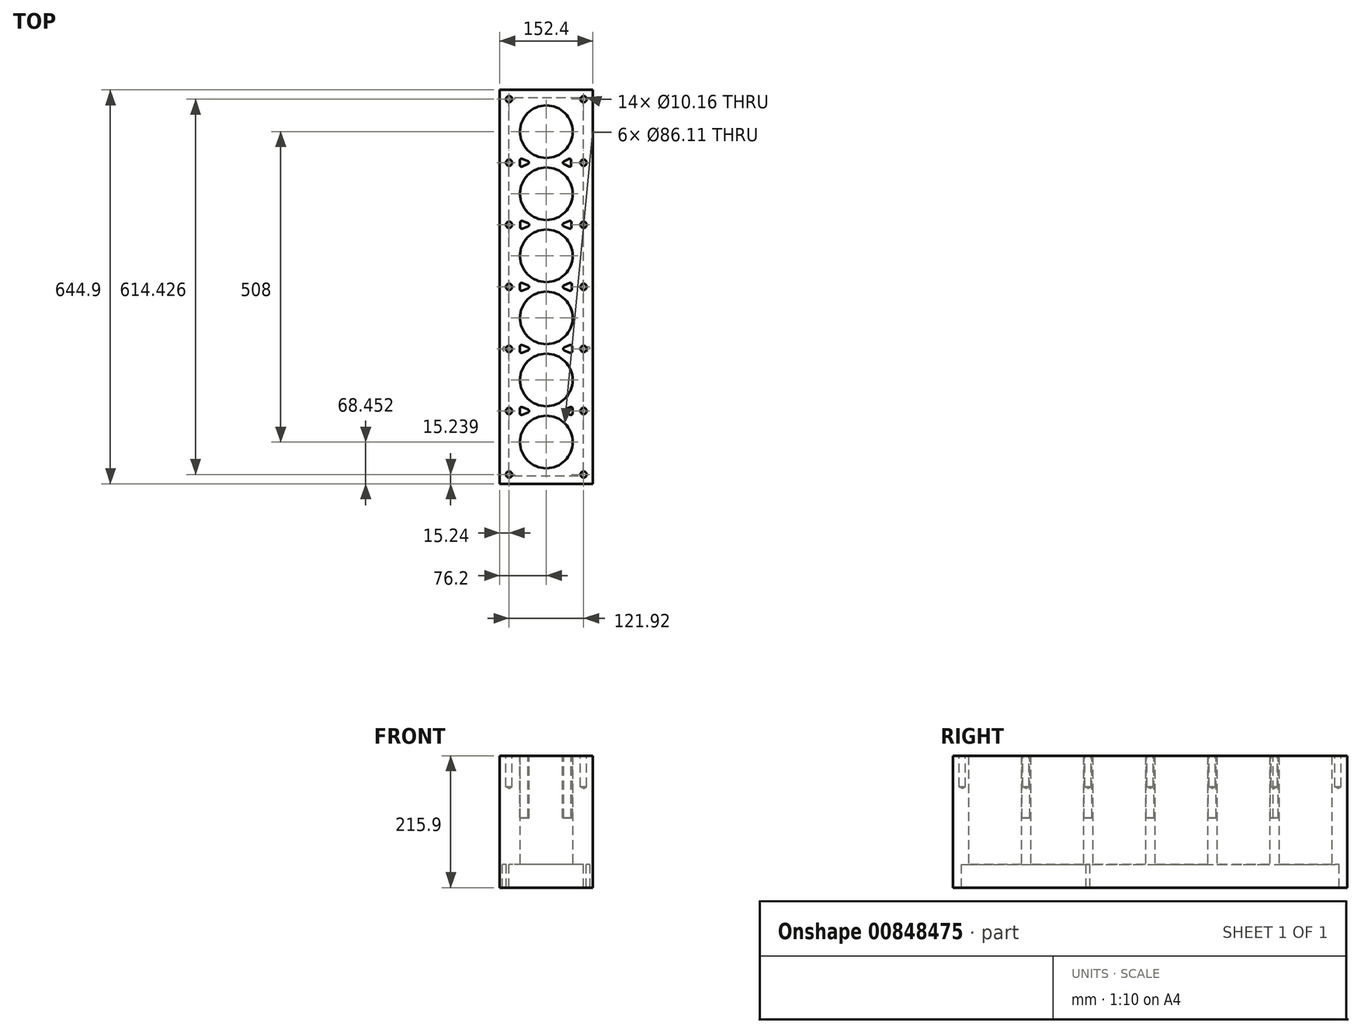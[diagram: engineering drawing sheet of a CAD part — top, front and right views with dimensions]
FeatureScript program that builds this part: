
annotation { "Feature Type Name" : "Feature", "Feature Type Description" : "" }
export const myFeature = defineFeature(function(context is Context, id is Id, definition is map)
    precondition{}
    {
        {
            var Q0;
            Q0=qCreatedBy(makeId("Top.planeOp"),FACE);
            var sketch = newSketch(context, id + "F0", { "sketchPlane" : qUnion([Q0])});
            skLineSegment(sketch, "E0.bottom", {"start": v(-76.2, 345.4) * mm, "end": v(76.2, 345.4) * mm});
            skLineSegment(sketch, "E0.top", {"start": v(-76.2, -299.5) * mm, "end": v(76.2, -299.5) * mm});
            skLineSegment(sketch, "E0.left", {"start": v(-76.2, 345.4) * mm, "end": v(-76.2, -299.5) * mm});
            skLineSegment(sketch, "E0.right", {"start": v(76.2, 345.4) * mm, "end": v(76.2, -299.5) * mm});
            skLineSegment(sketch, "E1", {"start": v(0, 345.4) * mm, "end": v(0, -299.5) * mm, "construction": true});
            skPoint(sketch, "E1.endSnap0", {"position": v(0, -299.5) * mm});
            skCircle(sketch, "E2", {"center": v(0, 276.95) * mm, "radius": 43.05 * mm});
            skCircle(sketch, "E3", {"center": v(0, 175.35) * mm, "radius": 43.05 * mm});
            skCircle(sketch, "E4", {"center": v(0, 73.75) * mm, "radius": 43.05 * mm});
            skCircle(sketch, "E5", {"center": v(0, -27.85) * mm, "radius": 43.05 * mm});
            skCircle(sketch, "E6", {"center": v(0, -129.45) * mm, "radius": 43.05 * mm});
            skCircle(sketch, "E7", {"center": v(0, -231.05) * mm, "radius": 43.05 * mm});
            skLineSegment(sketch, "E8", {"start": v(-76.2, 124.55) * mm, "end": v(0, 124.55) * mm, "construction": true});
            skLineSegment(sketch, "E9", {"start": v(0, 132.3) * mm, "end": v(-76.2, 132.3) * mm, "construction": true});
            skLineSegment(sketch, "E10", {"start": v(0, 233.9) * mm, "end": v(-76.2, 233.9) * mm, "construction": true});
            skLineSegment(sketch, "E11", {"start": v(-76.2, 226.15) * mm, "end": v(0, 226.15) * mm, "construction": true});
            skLineSegment(sketch, "E12", {"start": v(-76.2, 30.7) * mm, "end": v(0, 30.7) * mm, "construction": true});
            skLineSegment(sketch, "E13", {"start": v(0, 30.7) * mm, "end": v(0, 22.95) * mm, "construction": true});
            skLineSegment(sketch, "E14", {"start": v(0, 22.95) * mm, "end": v(-76.2, 22.95) * mm, "construction": true});
            skLineSegment(sketch, "E15", {"start": v(0, -70.9) * mm, "end": v(-76.2, -70.9) * mm, "construction": true});
            skLineSegment(sketch, "E16", {"start": v(-76.2, -78.65) * mm, "end": v(0, -78.65) * mm, "construction": true});
            skLineSegment(sketch, "E17", {"start": v(-76.2, -172.5) * mm, "end": v(0, -172.5) * mm, "construction": true});
            skLineSegment(sketch, "E18", {"start": v(-76.2, -180.25) * mm, "end": v(0, -180.25) * mm, "construction": true});
            skLineSegment(sketch, "E19", {"start": v(0, -180.25) * mm, "end": v(76.2, -180.25) * mm, "construction": true});
            skLineSegment(sketch, "E20", {"start": v(0, -172.5) * mm, "end": v(76.2, -172.5) * mm, "construction": true});
            skLineSegment(sketch, "E21", {"start": v(0, -78.65) * mm, "end": v(76.2, -78.65) * mm, "construction": true});
            skLineSegment(sketch, "E22", {"start": v(0, -70.9) * mm, "end": v(76.2, -70.9) * mm, "construction": true});
            skLineSegment(sketch, "E23", {"start": v(0, 22.95) * mm, "end": v(76.2, 22.95) * mm, "construction": true});
            skLineSegment(sketch, "E24", {"start": v(0, 30.7) * mm, "end": v(76.2, 30.7) * mm, "construction": true});
            skLineSegment(sketch, "E25", {"start": v(0, 124.55) * mm, "end": v(76.2, 124.55) * mm, "construction": true});
            skLineSegment(sketch, "E26", {"start": v(0, 132.3) * mm, "end": v(76.2, 132.3) * mm, "construction": true});
            skLineSegment(sketch, "E27", {"start": v(0, 226.15) * mm, "end": v(76.2, 226.15) * mm, "construction": true});
            skLineSegment(sketch, "E28", {"start": v(0, 233.9) * mm, "end": v(76.2, 233.9) * mm, "construction": true});
            skSolve(sketch);
        }
        {
            var Q0;
            Q0 = qSketchRegion(id + "F0", true);
            extrude(context, id + "F1", {"entities" : qUnion([Q0]), "depth" : 177.8 * mm, "offsetDistance" : 25.4 * mm});
        }
        {
            var Q0;
            Q0=makeQuery(id+"F1.opExtrude","CAP_FACE",FACE,{"disambiguationData":[OSD([sQuery(id+"F0.wireOp",EDGE,"E0.bottom"),sQuery(id+"F0.wireOp",EDGE,"E0.top"),sQuery(id+"F0.wireOp",EDGE,"E0.left"),sQuery(id+"F0.wireOp",EDGE,"E0.right"),sQuery(id+"F0.wireOp",EDGE,"E2"),sQuery(id+"F0.wireOp",EDGE,"E3"),sQuery(id+"F0.wireOp",EDGE,"E4"),sQuery(id+"F0.wireOp",EDGE,"E5"),sQuery(id+"F0.wireOp",EDGE,"E6"),sQuery(id+"F0.wireOp",EDGE,"E7")])],"isStart":false});
            var sketch = newSketch(context, id + "F2", { "sketchPlane" : qUnion([Q0])});
            skPoint(sketch, "E29", {"position": v(-60.96, 124.55) * mm});
            skPoint(sketch, "E30", {"position": v(-60.96, 330.16) * mm});
            skPoint(sketch, "E31", {"position": v(-60.96, 226.15) * mm});
            skPoint(sketch, "E32", {"position": v(-60.96, 22.95) * mm});
            skPoint(sketch, "E33", {"position": v(-60.96, -78.65) * mm});
            skPoint(sketch, "E34", {"position": v(-60.96, -180.25) * mm});
            skPoint(sketch, "E35", {"position": v(-60.96, -284.26) * mm});
            skPoint(sketch, "E36", {"position": v(60.96, -284.26) * mm});
            skPoint(sketch, "E37", {"position": v(60.96, -180.25) * mm});
            skPoint(sketch, "E38", {"position": v(60.96, 22.95) * mm});
            skPoint(sketch, "E39", {"position": v(60.96, 124.55) * mm});
            skPoint(sketch, "E40", {"position": v(60.96, 226.15) * mm});
            skPoint(sketch, "E41", {"position": v(60.96, 330.16) * mm});
            skLineSegment(sketch, "E42", {"start": v(-76.2, 345.4) * mm, "end": v(-76.2, -299.5) * mm, "construction": true});
            skLineSegment(sketch, "E43", {"start": v(0, 132.3) * mm, "end": v(76.2, 132.3) * mm, "construction": true});
            skLineSegment(sketch, "E44", {"start": v(76.2, 132.3) * mm, "end": v(-76.2, 132.3) * mm, "construction": true});
            skLineSegment(sketch, "E45", {"start": v(0, 116.8) * mm, "end": v(-76.2, 116.8) * mm, "construction": true});
            skLineSegment(sketch, "E46", {"start": v(0, 116.8) * mm, "end": v(76.2, 116.8) * mm, "construction": true});
            skLineSegment(sketch, "E47", {"start": v(0, 233.9) * mm, "end": v(-76.2, 233.9) * mm, "construction": true});
            skLineSegment(sketch, "E48", {"start": v(0, 233.9) * mm, "end": v(76.2, 233.9) * mm, "construction": true});
            skLineSegment(sketch, "E49", {"start": v(0, 218.4) * mm, "end": v(-76.2, 218.4) * mm, "construction": true});
            skLineSegment(sketch, "E50", {"start": v(0, 218.4) * mm, "end": v(76.2, 218.4) * mm, "construction": true});
            skLineSegment(sketch, "E51", {"start": v(76.2, 345.4) * mm, "end": v(76.2, -299.5) * mm, "construction": true});
            skLineSegment(sketch, "E52", {"start": v(0, 30.7) * mm, "end": v(-76.2, 30.7) * mm, "construction": true});
            skLineSegment(sketch, "E53", {"start": v(-76.2, 30.7) * mm, "end": v(76.2, 30.7) * mm, "construction": true});
            skLineSegment(sketch, "E54", {"start": v(0, 15.2) * mm, "end": v(-76.2, 15.2) * mm, "construction": true});
            skLineSegment(sketch, "E55", {"start": v(-76.2, 15.2) * mm, "end": v(76.2, 15.2) * mm, "construction": true});
            skLineSegment(sketch, "E56", {"start": v(0, -70.9) * mm, "end": v(-76.2, -70.9) * mm, "construction": true});
            skLineSegment(sketch, "E57", {"start": v(-76.2, -70.9) * mm, "end": v(76.2, -70.9) * mm, "construction": true});
            skLineSegment(sketch, "E58", {"start": v(0, -86.4) * mm, "end": v(-76.2, -86.4) * mm, "construction": true});
            skLineSegment(sketch, "E59", {"start": v(-76.2, -86.4) * mm, "end": v(76.2, -86.4) * mm, "construction": true});
            skPoint(sketch, "E60", {"position": v(60.96, -78.65) * mm});
            skLineSegment(sketch, "E61", {"start": v(0, -172.5) * mm, "end": v(-76.2, -172.5) * mm, "construction": true});
            skLineSegment(sketch, "E62", {"start": v(-76.2, -172.5) * mm, "end": v(76.2, -172.5) * mm, "construction": true});
            skLineSegment(sketch, "E63", {"start": v(0, -188) * mm, "end": v(-76.2, -188) * mm, "construction": true});
            skLineSegment(sketch, "E64", {"start": v(-76.2, -188) * mm, "end": v(76.2, -188) * mm, "construction": true});
            skSolve(sketch);
        }
        {
            var Q0;
            Q0=sQuery(id+"F2.wireOp",VERTEX,"E35");
            var Q1;
            Q1=sQuery(id+"F2.wireOp",VERTEX,"E36");
            var Q2;
            Q2=sQuery(id+"F2.wireOp",VERTEX,"E34");
            var Q3;
            Q3=sQuery(id+"F2.wireOp",VERTEX,"E37");
            var Q4;
            Q4=sQuery(id+"F2.wireOp",VERTEX,"E33");
            var Q5;
            Q5=sQuery(id+"F2.wireOp",VERTEX,"E60");
            var Q6;
            Q6=sQuery(id+"F2.wireOp",VERTEX,"E32");
            var Q7;
            Q7=sQuery(id+"F2.wireOp",VERTEX,"E38");
            var Q8;
            Q8=sQuery(id+"F2.wireOp",VERTEX,"E29");
            var Q9;
            Q9=sQuery(id+"F2.wireOp",VERTEX,"E39");
            var Q10;
            Q10=sQuery(id+"F2.wireOp",VERTEX,"E31");
            var Q11;
            Q11=sQuery(id+"F2.wireOp",VERTEX,"E40");
            var Q12;
            Q12=sQuery(id+"F2.wireOp",VERTEX,"E30");
            var Q13;
            Q13=sQuery(id+"F2.wireOp",VERTEX,"E41");
            var Q14;
            Q14=makeQuery(id+"F1.opExtrude","SWEPT_BODY",BODY,{"disambiguationData":[OSD([sQuery(id+"F0.wireOp",EDGE,"E0.bottom"),sQuery(id+"F0.wireOp",EDGE,"E0.top"),sQuery(id+"F0.wireOp",EDGE,"E0.left"),sQuery(id+"F0.wireOp",EDGE,"E0.right"),sQuery(id+"F0.wireOp",EDGE,"E2"),sQuery(id+"F0.wireOp",EDGE,"E3"),sQuery(id+"F0.wireOp",EDGE,"E4"),sQuery(id+"F0.wireOp",EDGE,"E5"),sQuery(id+"F0.wireOp",EDGE,"E6"),sQuery(id+"F0.wireOp",EDGE,"E7")])]});
            hole(context, id + "F3", {"style" : HoleStyle.SIMPLE, "endStyle" : HoleEndStyle.BLIND, "holeDiameter" : 10.16 * mm, "majorDiameter" : 6.35 * mm, "holeDepth" : 50.8 * mm, "isTappedThrough" : true, "tappedDepth" : 12.7 * mm, "tapClearance" : 3, "locations" : qUnion([Q0, Q1, Q2, Q3, Q4, Q5, Q6, Q7, Q8, Q9, Q10, Q11, Q12, Q13]), "scope" : qUnion([Q14])});
        }
        {
            var Q0;
            Q0=makeQuery(id+"F1.opExtrude","CAP_FACE",FACE,{"disambiguationData":[OSD([sQuery(id+"F0.wireOp",EDGE,"E0.bottom"),sQuery(id+"F0.wireOp",EDGE,"E0.top"),sQuery(id+"F0.wireOp",EDGE,"E0.left"),sQuery(id+"F0.wireOp",EDGE,"E0.right"),sQuery(id+"F0.wireOp",EDGE,"E2"),sQuery(id+"F0.wireOp",EDGE,"E3"),sQuery(id+"F0.wireOp",EDGE,"E4"),sQuery(id+"F0.wireOp",EDGE,"E5"),sQuery(id+"F0.wireOp",EDGE,"E6"),sQuery(id+"F0.wireOp",EDGE,"E7")])],"isStart":false});
            var sketch = newSketch(context, id + "F4", { "sketchPlane" : qUnion([Q0])});
            skLineSegment(sketch, "E65", {"start": v(0, 233.9) * mm, "end": v(-76.2, 233.9) * mm, "construction": true});
            skLineSegment(sketch, "E66", {"start": v(-76.2, 233.9) * mm, "end": v(76.2, 233.9) * mm, "construction": true});
            skLineSegment(sketch, "E67", {"start": v(0, 218.4) * mm, "end": v(-76.2, 218.4) * mm, "construction": true});
            skLineSegment(sketch, "E68", {"start": v(-76.2, 218.4) * mm, "end": v(76.2, 218.4) * mm, "construction": true});
            skLineSegment(sketch, "E69", {"start": v(40.28, 292.16) * mm, "end": v(43.05, -230.82) * mm, "construction": true});
            skLineSegment(sketch, "E70", {"start": v(40.6, 230.23) * mm, "end": v(40.65, 222.1) * mm});
            skLineSegment(sketch, "E71", {"start": v(-76.2, 226.15) * mm, "end": v(76.2, 226.15) * mm, "construction": true});
            skLineSegment(sketch, "E72", {"start": v(37.27, 232.33) * mm, "end": v(28.7, 228.27) * mm});
            skLineSegment(sketch, "E73", {"start": v(28.7, 224.04) * mm, "end": v(37.32, 219.98) * mm});
            skLineSegment(sketch, "E74", {"start": v(0, 132.3) * mm, "end": v(-76.2, 132.3) * mm, "construction": true});
            skLineSegment(sketch, "E75", {"start": v(0, 132.3) * mm, "end": v(76.2, 132.3) * mm, "construction": true});
            skLineSegment(sketch, "E76", {"start": v(0, 116.8) * mm, "end": v(-76.2, 116.8) * mm, "construction": true});
            skLineSegment(sketch, "E77", {"start": v(0, 116.8) * mm, "end": v(76.2, 116.8) * mm, "construction": true});
            skLineSegment(sketch, "E78", {"start": v(-76.2, 124.55) * mm, "end": v(76.2, 124.55) * mm, "construction": true});
            skLineSegment(sketch, "E79", {"start": v(-42.75, 128.5) * mm, "end": v(-42.73, 120.6) * mm});
            skLineSegment(sketch, "E80", {"start": v(-39.22, 118.25) * mm, "end": v(-29.64, 122.2) * mm});
            skLineSegment(sketch, "E81", {"start": v(-29.64, 126.9) * mm, "end": v(-39.24, 130.85) * mm});
            skPoint(sketch, "E82.visualSharp", {"position": v(-23.94, 124.55) * mm});
            skArc(sketch, "E82.filletArc", {"start": v(-29.64, 122.2) * mm, "mid": v(-28.06, 124.55) * mm, "end": v(-29.64, 126.9) * mm});
            skPoint(sketch, "E83.visualSharp", {"position": v(-42.75, 132.3) * mm});
            skArc(sketch, "E83.filletArc", {"start": v(-39.24, 130.85) * mm, "mid": v(-41.62, 130.61) * mm, "end": v(-42.75, 128.5) * mm});
            skPoint(sketch, "E84.visualSharp", {"position": v(-42.72, 116.8) * mm});
            skArc(sketch, "E84.filletArc", {"start": v(-42.73, 120.6) * mm, "mid": v(-41.6, 118.48) * mm, "end": v(-39.22, 118.25) * mm});
            skPoint(sketch, "E85.visualSharp", {"position": v(-24.18, 226.15) * mm});
            skArc(sketch, "E85.filletArc", {"start": v(-29.87, 224.18) * mm, "mid": v(-28.42, 226.34) * mm, "end": v(-29.87, 228.5) * mm});
            skPoint(sketch, "E86.visualSharp", {"position": v(40.59, 233.9) * mm});
            skArc(sketch, "E86.filletArc", {"start": v(40.6, 230.23) * mm, "mid": v(39.52, 232.2) * mm, "end": v(37.27, 232.33) * mm});
            skPoint(sketch, "E87.visualSharp", {"position": v(40.67, 218.4) * mm});
            skArc(sketch, "E87.filletArc", {"start": v(37.32, 219.98) * mm, "mid": v(39.57, 220.13) * mm, "end": v(40.65, 222.1) * mm});
            skPoint(sketch, "E88.visualSharp", {"position": v(24.24, 226.15) * mm});
            skArc(sketch, "E88.filletArc", {"start": v(28.7, 228.27) * mm, "mid": v(27.37, 226.15) * mm, "end": v(28.7, 224.04) * mm});
            skLineSegment(sketch, "E89", {"start": v(-43.04, 278.07) * mm, "end": v(-43.04, -232.17) * mm, "construction": true});
            skLineSegment(sketch, "E90", {"start": v(-43.04, 230.11) * mm, "end": v(-43.04, 222.3) * mm});
            skLineSegment(sketch, "E91", {"start": v(-39.48, 219.97) * mm, "end": v(-29.87, 224.18) * mm});
            skLineSegment(sketch, "E92", {"start": v(-39.53, 232.46) * mm, "end": v(-29.87, 228.5) * mm});
            skPoint(sketch, "E93.visualSharp", {"position": v(-43.04, 233.9) * mm});
            skArc(sketch, "E93.filletArc", {"start": v(-39.53, 232.46) * mm, "mid": v(-41.91, 232.22) * mm, "end": v(-43.04, 230.11) * mm});
            skPoint(sketch, "E94.visualSharp", {"position": v(-43.04, 218.4) * mm});
            skArc(sketch, "E94.filletArc", {"start": v(-43.04, 222.3) * mm, "mid": v(-41.89, 220.17) * mm, "end": v(-39.48, 219.97) * mm});
            skLineSegment(sketch, "E95", {"start": v(41.13, 128.54) * mm, "end": v(41.13, 120.56) * mm});
            skLineSegment(sketch, "E96", {"start": v(37.67, 118.27) * mm, "end": v(28.26, 122.26) * mm});
            skLineSegment(sketch, "E97", {"start": v(28.26, 126.84) * mm, "end": v(37.67, 130.83) * mm});
            skPoint(sketch, "E98.visualSharp", {"position": v(22.85, 124.55) * mm});
            skArc(sketch, "E98.filletArc", {"start": v(28.26, 126.84) * mm, "mid": v(26.74, 124.55) * mm, "end": v(28.26, 122.26) * mm});
            skPoint(sketch, "E99.visualSharp", {"position": v(41.13, 132.3) * mm});
            skArc(sketch, "E99.filletArc", {"start": v(41.13, 128.54) * mm, "mid": v(40.01, 130.62) * mm, "end": v(37.67, 130.83) * mm});
            skPoint(sketch, "E100.visualSharp", {"position": v(41.13, 116.8) * mm});
            skArc(sketch, "E100.filletArc", {"start": v(37.67, 118.27) * mm, "mid": v(40.01, 118.49) * mm, "end": v(41.13, 120.56) * mm});
            skLineSegment(sketch, "E101", {"start": v(0, 30.7) * mm, "end": v(-76.2, 30.7) * mm, "construction": true});
            skLineSegment(sketch, "E102", {"start": v(0, 30.7) * mm, "end": v(76.2, 30.7) * mm, "construction": true});
            skLineSegment(sketch, "E103", {"start": v(0, 15.2) * mm, "end": v(76.2, 15.2) * mm, "construction": true});
            skLineSegment(sketch, "E104", {"start": v(0, 15.2) * mm, "end": v(-76.2, 15.2) * mm, "construction": true});
            skLineSegment(sketch, "E105", {"start": v(-76.2, 22.95) * mm, "end": v(76.2, 22.95) * mm, "construction": true});
            skLineSegment(sketch, "E106", {"start": v(-43.04, 26.9) * mm, "end": v(-43.04, 19) * mm});
            skPoint(sketch, "E106.endSnap0", {"position": v(-38.1, 15.2) * mm});
            skLineSegment(sketch, "E107", {"start": v(-39.53, 16.65) * mm, "end": v(-29.95, 20.6) * mm});
            skLineSegment(sketch, "E108", {"start": v(-29.95, 25.3) * mm, "end": v(-39.53, 29.25) * mm});
            skPoint(sketch, "E109.visualSharp", {"position": v(-43.04, 30.7) * mm});
            skArc(sketch, "E109.filletArc", {"start": v(-39.53, 29.25) * mm, "mid": v(-41.91, 29.01) * mm, "end": v(-43.04, 26.9) * mm});
            skPoint(sketch, "E110.visualSharp", {"position": v(-43.04, 15.2) * mm});
            skArc(sketch, "E110.filletArc", {"start": v(-43.04, 19) * mm, "mid": v(-41.91, 16.89) * mm, "end": v(-39.53, 16.65) * mm});
            skPoint(sketch, "E111.visualSharp", {"position": v(-24.25, 22.95) * mm});
            skArc(sketch, "E111.filletArc", {"start": v(-29.95, 20.6) * mm, "mid": v(-28.38, 22.95) * mm, "end": v(-29.95, 25.3) * mm});
            skLineSegment(sketch, "E112", {"start": v(41.69, 26.95) * mm, "end": v(41.73, 19) * mm});
            skLineSegment(sketch, "E113", {"start": v(38.25, 16.67) * mm, "end": v(28.8, 20.65) * mm});
            skLineSegment(sketch, "E114", {"start": v(38.2, 29.24) * mm, "end": v(28.79, 25.26) * mm});
            skPoint(sketch, "E115.visualSharp", {"position": v(23.3, 22.95) * mm});
            skArc(sketch, "E115.filletArc", {"start": v(28.79, 25.26) * mm, "mid": v(27.26, 22.95) * mm, "end": v(28.8, 20.65) * mm});
            skPoint(sketch, "E116.visualSharp", {"position": v(41.67, 30.7) * mm});
            skArc(sketch, "E116.filletArc", {"start": v(41.69, 26.95) * mm, "mid": v(40.56, 29.02) * mm, "end": v(38.2, 29.24) * mm});
            skPoint(sketch, "E117.visualSharp", {"position": v(41.75, 15.2) * mm});
            skArc(sketch, "E117.filletArc", {"start": v(38.25, 16.67) * mm, "mid": v(40.62, 16.9) * mm, "end": v(41.73, 19) * mm});
            skLineSegment(sketch, "E118", {"start": v(0, -70.9) * mm, "end": v(-76.2, -70.9) * mm, "construction": true});
            skLineSegment(sketch, "E119", {"start": v(0, -70.9) * mm, "end": v(76.2, -70.9) * mm, "construction": true});
            skLineSegment(sketch, "E120", {"start": v(0, -86.4) * mm, "end": v(-76.2, -86.4) * mm, "construction": true});
            skLineSegment(sketch, "E121", {"start": v(0, -86.4) * mm, "end": v(76.2, -86.4) * mm, "construction": true});
            skLineSegment(sketch, "E122", {"start": v(-76.2, -78.65) * mm, "end": v(76.2, -78.65) * mm, "construction": true});
            skLineSegment(sketch, "E123", {"start": v(-43.04, -74.7) * mm, "end": v(-43.04, -82.6) * mm});
            skLineSegment(sketch, "E124", {"start": v(-39.53, -84.95) * mm, "end": v(-29.95, -81) * mm});
            skLineSegment(sketch, "E125", {"start": v(-29.95, -76.3) * mm, "end": v(-39.53, -72.35) * mm});
            skPoint(sketch, "E126.visualSharp", {"position": v(-43.04, -70.9) * mm});
            skArc(sketch, "E126.filletArc", {"start": v(-39.53, -72.35) * mm, "mid": v(-41.91, -72.59) * mm, "end": v(-43.04, -74.7) * mm});
            skPoint(sketch, "E127.visualSharp", {"position": v(-43.04, -86.4) * mm});
            skArc(sketch, "E127.filletArc", {"start": v(-43.04, -82.6) * mm, "mid": v(-41.91, -84.71) * mm, "end": v(-39.53, -84.95) * mm});
            skPoint(sketch, "E128.visualSharp", {"position": v(-24.25, -78.65) * mm});
            skArc(sketch, "E128.filletArc", {"start": v(-29.95, -81) * mm, "mid": v(-28.38, -78.65) * mm, "end": v(-29.95, -76.3) * mm});
            skLineSegment(sketch, "E129", {"start": v(42.22, -74.69) * mm, "end": v(42.27, -82.57) * mm});
            skLineSegment(sketch, "E130", {"start": v(38.75, -84.94) * mm, "end": v(29.16, -81) * mm});
            skLineSegment(sketch, "E131", {"start": v(29.15, -76.29) * mm, "end": v(38.7, -72.35) * mm});
            skPoint(sketch, "E132.visualSharp", {"position": v(23.43, -78.65) * mm});
            skArc(sketch, "E132.filletArc", {"start": v(29.15, -76.29) * mm, "mid": v(27.58, -78.65) * mm, "end": v(29.16, -81) * mm});
            skPoint(sketch, "E133.visualSharp", {"position": v(42.2, -70.9) * mm});
            skArc(sketch, "E133.filletArc", {"start": v(42.22, -74.69) * mm, "mid": v(41.09, -72.58) * mm, "end": v(38.7, -72.35) * mm});
            skPoint(sketch, "E134.visualSharp", {"position": v(42.29, -86.4) * mm});
            skArc(sketch, "E134.filletArc", {"start": v(38.75, -84.94) * mm, "mid": v(41.14, -84.7) * mm, "end": v(42.27, -82.57) * mm});
            skLineSegment(sketch, "E135", {"start": v(0, -172.5) * mm, "end": v(-76.2, -172.5) * mm, "construction": true});
            skLineSegment(sketch, "E136", {"start": v(0, -172.5) * mm, "end": v(76.2, -172.5) * mm, "construction": true});
            skLineSegment(sketch, "E137", {"start": v(0, -188) * mm, "end": v(-76.2, -188) * mm, "construction": true});
            skLineSegment(sketch, "E138", {"start": v(0, -188) * mm, "end": v(76.2, -188) * mm, "construction": true});
            skLineSegment(sketch, "E139", {"start": v(-76.2, -180.25) * mm, "end": v(76.2, -180.25) * mm, "construction": true});
            skLineSegment(sketch, "E140", {"start": v(-43.04, -176.3) * mm, "end": v(-43.04, -184.2) * mm});
            skLineSegment(sketch, "E141", {"start": v(-39.53, -186.55) * mm, "end": v(-29.95, -182.6) * mm});
            skLineSegment(sketch, "E142", {"start": v(-29.95, -177.9) * mm, "end": v(-39.53, -173.95) * mm});
            skLineSegment(sketch, "E143", {"start": v(42.76, -176.28) * mm, "end": v(42.8, -184.18) * mm});
            skLineSegment(sketch, "E144", {"start": v(39.3, -186.54) * mm, "end": v(29.72, -182.6) * mm});
            skLineSegment(sketch, "E145", {"start": v(29.72, -177.9) * mm, "end": v(39.25, -173.95) * mm});
            skPoint(sketch, "E146.visualSharp", {"position": v(-24.25, -180.25) * mm});
            skArc(sketch, "E146.filletArc", {"start": v(-29.95, -182.6) * mm, "mid": v(-28.38, -180.25) * mm, "end": v(-29.95, -177.9) * mm});
            skPoint(sketch, "E147.visualSharp", {"position": v(24.04, -180.25) * mm});
            skArc(sketch, "E147.filletArc", {"start": v(29.72, -177.9) * mm, "mid": v(28.15, -180.25) * mm, "end": v(29.72, -182.6) * mm});
            skPoint(sketch, "E148.visualSharp", {"position": v(42.74, -172.5) * mm});
            skArc(sketch, "E148.filletArc", {"start": v(42.76, -176.28) * mm, "mid": v(41.63, -174.18) * mm, "end": v(39.25, -173.95) * mm});
            skPoint(sketch, "E149.visualSharp", {"position": v(42.83, -188) * mm});
            skArc(sketch, "E149.filletArc", {"start": v(39.3, -186.54) * mm, "mid": v(41.68, -186.3) * mm, "end": v(42.8, -184.18) * mm});
            skPoint(sketch, "E150.visualSharp", {"position": v(-43.04, -188) * mm});
            skArc(sketch, "E150.filletArc", {"start": v(-43.04, -184.2) * mm, "mid": v(-41.91, -186.31) * mm, "end": v(-39.53, -186.55) * mm});
            skPoint(sketch, "E151.visualSharp", {"position": v(-43.04, -172.5) * mm});
            skArc(sketch, "E151.filletArc", {"start": v(-39.53, -173.95) * mm, "mid": v(-41.91, -174.19) * mm, "end": v(-43.04, -176.3) * mm});
            skSolve(sketch);
        }
        {
            var Q0;
            Q0=makeQuery(id+"F4.imprint","IMPRINT",FACE,{"disambiguationData":[TD([[makeQuery(id+"F4.imprint","IMPRINT",EDGE,{"derivedFrom":sQuery(id+"F4.wireOp",EDGE,"E140")}),1.0]])]});
            var Q1;
            Q1=makeQuery(id+"F4.imprint","IMPRINT",FACE,{"disambiguationData":[TD([[makeQuery(id+"F4.imprint","IMPRINT",EDGE,{"derivedFrom":sQuery(id+"F4.wireOp",EDGE,"E143")}),-1.0]])]});
            var Q2;
            Q2=makeQuery(id+"F4.imprint","IMPRINT",FACE,{"disambiguationData":[TD([[makeQuery(id+"F4.imprint","IMPRINT",EDGE,{"derivedFrom":sQuery(id+"F4.wireOp",EDGE,"E123")}),1.0]])]});
            var Q3;
            Q3=makeQuery(id+"F4.imprint","IMPRINT",FACE,{"disambiguationData":[TD([[makeQuery(id+"F4.imprint","IMPRINT",EDGE,{"derivedFrom":sQuery(id+"F4.wireOp",EDGE,"E129")}),-1.0]])]});
            var Q4;
            Q4=makeQuery(id+"F4.imprint","IMPRINT",FACE,{"disambiguationData":[TD([[makeQuery(id+"F4.imprint","IMPRINT",EDGE,{"derivedFrom":sQuery(id+"F4.wireOp",EDGE,"E106")}),1.0]])]});
            var Q5;
            Q5=makeQuery(id+"F4.imprint","IMPRINT",FACE,{"disambiguationData":[TD([[makeQuery(id+"F4.imprint","IMPRINT",EDGE,{"derivedFrom":sQuery(id+"F4.wireOp",EDGE,"E112")}),-1.0]])]});
            var Q6;
            Q6=makeQuery(id+"F4.imprint","IMPRINT",FACE,{"disambiguationData":[TD([[makeQuery(id+"F4.imprint","IMPRINT",EDGE,{"derivedFrom":sQuery(id+"F4.wireOp",EDGE,"E79")}),1.0]])]});
            var Q7;
            Q7=makeQuery(id+"F4.imprint","IMPRINT",FACE,{"disambiguationData":[TD([[makeQuery(id+"F4.imprint","IMPRINT",EDGE,{"derivedFrom":sQuery(id+"F4.wireOp",EDGE,"E95")}),-1.0]])]});
            var Q8;
            Q8=makeQuery(id+"F4.imprint","IMPRINT",FACE,{"disambiguationData":[TD([[makeQuery(id+"F4.imprint","IMPRINT",EDGE,{"derivedFrom":sQuery(id+"F4.wireOp",EDGE,"E85.filletArc")}),1.0]])]});
            var Q9;
            Q9=makeQuery(id+"F4.imprint","IMPRINT",FACE,{"disambiguationData":[TD([[makeQuery(id+"F4.imprint","IMPRINT",EDGE,{"derivedFrom":sQuery(id+"F4.wireOp",EDGE,"E70")}),-1.0]])]});
            extrude(context, id + "F5", {"entities" : qUnion([Q0, Q1, Q2, Q3, Q4, Q5, Q6, Q7, Q8, Q9]), "operationType" : NewBodyOperationType.REMOVE, "oppositeDirection" : true, "depth" : 101.6 * mm, "offsetDistance" : 25.4 * mm});
        }
        {
            var Q0;
            Q0=makeQuery(id+"F1.opExtrude","CAP_FACE",FACE,{"disambiguationData":[OSD([sQuery(id+"F0.wireOp",EDGE,"E0.bottom"),sQuery(id+"F0.wireOp",EDGE,"E0.top"),sQuery(id+"F0.wireOp",EDGE,"E0.left"),sQuery(id+"F0.wireOp",EDGE,"E0.right"),sQuery(id+"F0.wireOp",EDGE,"E2"),sQuery(id+"F0.wireOp",EDGE,"E3"),sQuery(id+"F0.wireOp",EDGE,"E4"),sQuery(id+"F0.wireOp",EDGE,"E5"),sQuery(id+"F0.wireOp",EDGE,"E6"),sQuery(id+"F0.wireOp",EDGE,"E7")])],"isStart":true});
            var sketch = newSketch(context, id + "F6", { "sketchPlane" : qUnion([Q0])});
            skPoint(sketch, "E152", {"position": v(-63.45, -124.53) * mm});
            skPoint(sketch, "E153", {"position": v(-63.48, -332.65) * mm});
            skPoint(sketch, "E154", {"position": v(63.53, -124.57) * mm});
            skPoint(sketch, "E155", {"position": v(60.89, -332.11) * mm});
            skPoint(sketch, "E156", {"position": v(-63.47, 78.61) * mm});
            skPoint(sketch, "E157", {"position": v(63.52, 78.62) * mm});
            skPoint(sketch, "E158", {"position": v(-63.4, 286.63) * mm});
            skPoint(sketch, "E159", {"position": v(63.4, 286.62) * mm});
            skSolve(sketch);
        }
        {
            var Q0;
            Q0=makeQuery(id+"F6.imprint","IMPRINT",FACE,{"disambiguationData":[TD([[makeQuery(id+"F6.imprint","IMPRINT",EDGE,{"derivedFrom":makeQuery(id+"F1.opExtrude","CAP_EDGE",EDGE,{"disambiguationData":[OSD([sQuery(id+"F0.wireOp",EDGE,"E0.bottom")])],"isStart":true})}),1.0]])]});
            var sketch = newSketch(context, id + "F7", { "sketchPlane" : qUnion([Q0])});
            skLineSegment(sketch, "E160", {"start": v(-60.96, 286.06) * mm, "end": v(-60.96, -321.84) * mm});
            skLineSegment(sketch, "E161", {"start": v(-60.96, 286.06) * mm, "end": v(60.96, 286.06) * mm});
            skLineSegment(sketch, "E162", {"start": v(60.96, 286.06) * mm, "end": v(60.96, -331.97) * mm});
            skLineSegment(sketch, "E163", {"start": v(60.96, -331.97) * mm, "end": v(-60.96, -331.97) * mm});
            skLineSegment(sketch, "E164", {"start": v(-60.96, -321.84) * mm, "end": v(-60.96, -331.97) * mm});
            skPoint(sketch, "E165", {"position": v(-68.58, 78.65) * mm});
            skPoint(sketch, "E166", {"position": v(68.58, 78.65) * mm});
            skLineSegment(sketch, "E167", {"start": v(76.35, 299.5) * mm, "end": v(76.35, -345.4) * mm});
            skLineSegment(sketch, "E168", {"start": v(-76.2, -345.4) * mm, "end": v(76.35, -345.4) * mm});
            skLineSegment(sketch, "E169", {"start": v(76.35, 299.5) * mm, "end": v(-76.05, 299.5) * mm});
            skPoint(sketch, "E170", {"position": v(0, 292.78) * mm});
            skPoint(sketch, "E171", {"position": v(-68.58, 292.78) * mm});
            skPoint(sketch, "E172", {"position": v(68.73, 292.78) * mm});
            skPoint(sketch, "E173", {"position": v(-68.58, 229.28) * mm});
            skPoint(sketch, "E174", {"position": v(-68.58, 178.48) * mm});
            skPoint(sketch, "E175", {"position": v(-68.86, 127.68) * mm});
            skPoint(sketch, "E176", {"position": v(-68.9, 27.85) * mm});
            skPoint(sketch, "E177", {"position": v(-68.7, -22.95) * mm});
            skPoint(sketch, "E178", {"position": v(-68.74, -73.75) * mm});
            skPoint(sketch, "E179", {"position": v(-68.65, -124.55) * mm});
            skPoint(sketch, "E180", {"position": v(-69.13, -175.35) * mm});
            skPoint(sketch, "E181", {"position": v(-68.78, -226.15) * mm});
            skPoint(sketch, "E182", {"position": v(-69.1, -276.95) * mm});
            skPoint(sketch, "E183", {"position": v(0, -338.69) * mm});
            skPoint(sketch, "E184", {"position": v(68.73, -338.69) * mm});
            skPoint(sketch, "E185", {"position": v(-68.58, -338.69) * mm});
            skPoint(sketch, "E186", {"position": v(68.58, 229.28) * mm});
            skPoint(sketch, "E187", {"position": v(68.58, 178.48) * mm});
            skPoint(sketch, "E188", {"position": v(68.58, 127.68) * mm});
            skPoint(sketch, "E189", {"position": v(68.58, 27.85) * mm});
            skPoint(sketch, "E190", {"position": v(68.58, -22.95) * mm});
            skPoint(sketch, "E191", {"position": v(68.58, -73.75) * mm});
            skPoint(sketch, "E192", {"position": v(68.58, -124.55) * mm});
            skPoint(sketch, "E193", {"position": v(68.58, -175.35) * mm});
            skPoint(sketch, "E194", {"position": v(68.58, -226.15) * mm});
            skPoint(sketch, "E195", {"position": v(68.58, -276.95) * mm});
            skSolve(sketch);
        }
        {
            var Q0;
            Q0=makeQuery(id+"F7.imprint","IMPRINT",FACE,{"disambiguationData":[TD([[makeQuery(id+"F7.imprint","IMPRINT",EDGE,{"derivedFrom":sQuery(id+"F7.wireOp",EDGE,"E160")}),-1.0]])]});
            extrude(context, id + "F8", {"entities" : qUnion([Q0]), "operationType" : NewBodyOperationType.ADD, "depth" : 38.1 * mm, "offsetDistance" : 25.4 * mm});
        }
        {
            var Q0;
            Q0=sQuery(id+"F7.wireOp",VERTEX,"79ca7677-756c-4831-aa4d-dab98c900ab2");
            var Q1;
            Q1=sQuery(id+"F7.wireOp",VERTEX,"E165");
            var Q2;
            Q2=sQuery(id+"F7.wireOp",VERTEX,"E166");
            var Q3;
            Q3=sQuery(id+"F7.wireOp",VERTEX,"900c452b-c8c2-43f0-92fa-25178b32092c");
            var Q4;
            Q4=sQuery(id+"F7.wireOp",VERTEX,"5c776b35-4e05-4b04-9218-bed21588f697");
            var Q5;
            Q5=sQuery(id+"F7.wireOp",VERTEX,"8d4a5477-1d21-4aaa-8465-e8d8f552d7ef");
            var Q6;
            Q6=sQuery(id+"F7.wireOp",VERTEX,"2076e362-e182-4081-8048-38b1c2610852");
            var Q7;
            Q7=sQuery(id+"F7.wireOp",VERTEX,"c9698c75-6f65-45ff-bf80-3e5c7173e084");
            var Q8;
            Q8=makeQuery(id+"F1.opExtrude","SWEPT_BODY",BODY,{"disambiguationData":[OSD([sQuery(id+"F0.wireOp",EDGE,"E0.bottom"),sQuery(id+"F0.wireOp",EDGE,"E0.top"),sQuery(id+"F0.wireOp",EDGE,"E0.left"),sQuery(id+"F0.wireOp",EDGE,"E0.right"),sQuery(id+"F0.wireOp",EDGE,"E2"),sQuery(id+"F0.wireOp",EDGE,"E3"),sQuery(id+"F0.wireOp",EDGE,"E4"),sQuery(id+"F0.wireOp",EDGE,"E5"),sQuery(id+"F0.wireOp",EDGE,"E6"),sQuery(id+"F0.wireOp",EDGE,"E7")])]});
            hole(context, id + "F9", {"style" : HoleStyle.SIMPLE, "endStyle" : HoleEndStyle.BLIND, "oppositeDirection" : true, "holeDiameter" : 6.35 * mm, "majorDiameter" : 6.35 * mm, "holeDepth" : 38.1 * mm, "isTappedThrough" : true, "tappedDepth" : 12.7 * mm, "tapClearance" : 3, "locations" : qUnion([Q0, Q1, Q2, Q3, Q4, Q5, Q6, Q7]), "scope" : qUnion([Q8])});
        }
        {
            var Q0;
            Q0=makeQuery(id+"F8.opExtrude","SWEPT_EDGE",EDGE,{"disambiguationData":[OSD([sQuery(id+"F7.wireOp",EDGE,"E161"),sQuery(id+"F7.wireOp",EDGE,"E162")])]});
            var Q1;
            Q1=makeQuery(id+"F8.opExtrude","SWEPT_EDGE",EDGE,{"disambiguationData":[OSD([sQuery(id+"F7.wireOp",EDGE,"E160"),sQuery(id+"F7.wireOp",EDGE,"E161")])]});
            var Q2;
            Q2=makeQuery(id+"F8.opExtrude","SWEPT_EDGE",EDGE,{"disambiguationData":[OSD([sQuery(id+"F7.wireOp",EDGE,"E162"),sQuery(id+"F7.wireOp",EDGE,"E163")])]});
            var Q3;
            Q3=makeQuery(id+"F8.opExtrude","SWEPT_EDGE",EDGE,{"disambiguationData":[OSD([sQuery(id+"F7.wireOp",EDGE,"E163"),sQuery(id+"F7.wireOp",EDGE,"E164")])]});
            fillet(context, id + "F10", {"entities" : qUnion([Q0, Q1, Q2, Q3]), "radius" : 6.35 * mm, "tangentPropagation" : true, "allowEdgeOverflow" : false});
        }
    });
